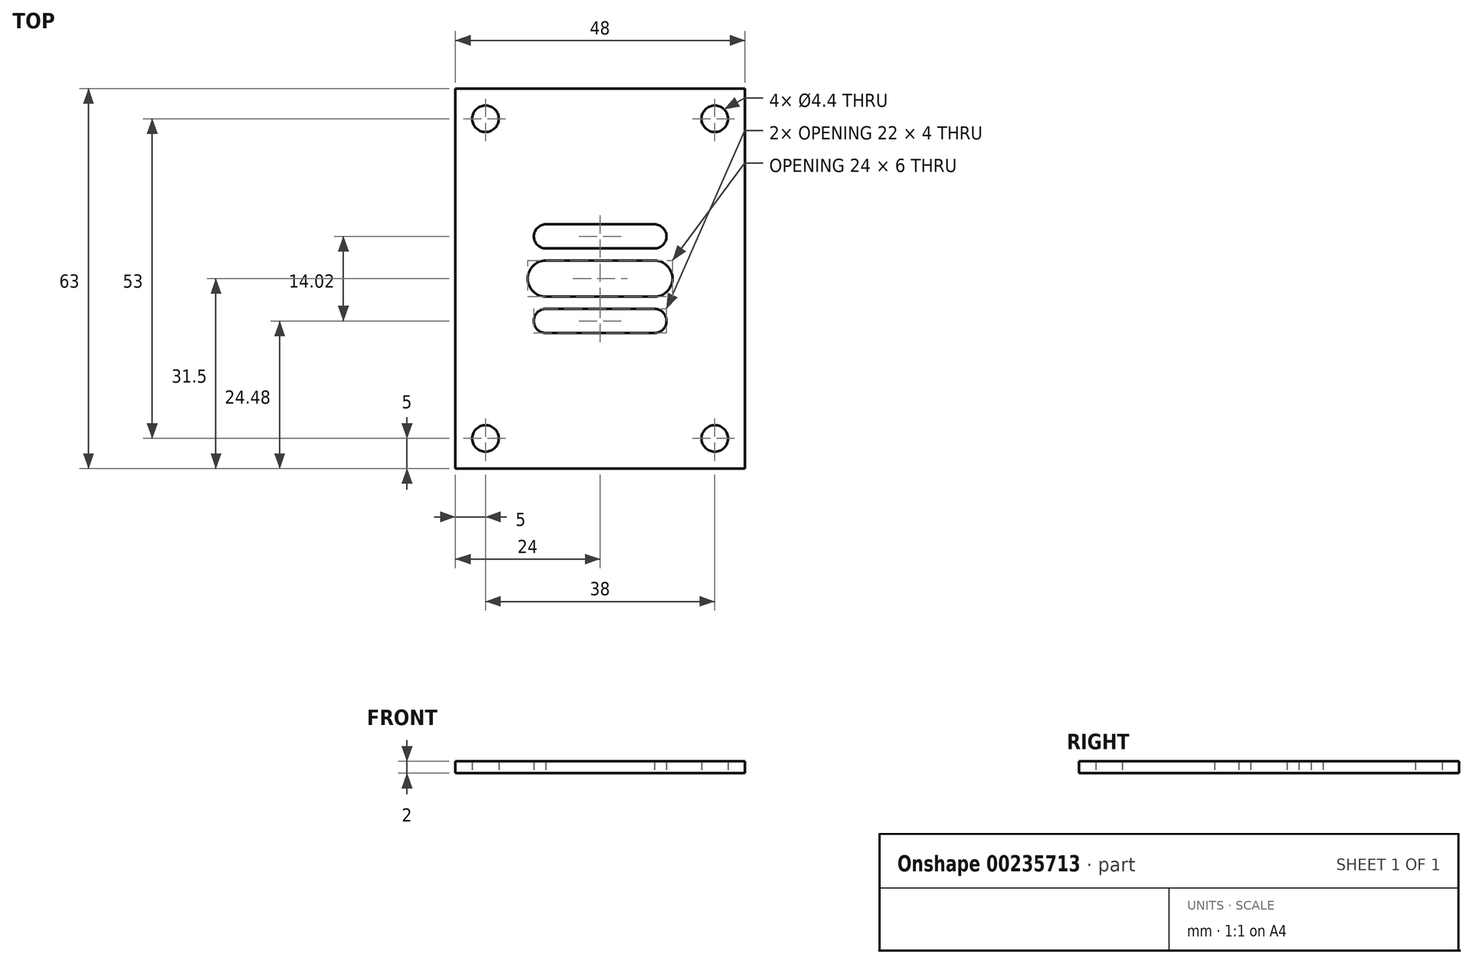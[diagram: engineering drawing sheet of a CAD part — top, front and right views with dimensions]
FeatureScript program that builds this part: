
annotation { "Feature Type Name" : "Feature", "Feature Type Description" : "" }
export const myFeature = defineFeature(function(context is Context, id is Id, definition is map)
    precondition{}
    {
        {
            var Q0;
            Q0=qCreatedBy(makeId("Top.planeOp"),FACE);
            var sketch = newSketch(context, id + "F0", { "sketchPlane" : qUnion([Q0])});
            skLineSegment(sketch, "E0.bottom", {"start": v(0, 0) * mm, "end": v(48, 0) * mm});
            skLineSegment(sketch, "E0.top", {"start": v(0, -63) * mm, "end": v(48, -63) * mm});
            skLineSegment(sketch, "E0.left", {"start": v(0, 0) * mm, "end": v(0, -63) * mm});
            skLineSegment(sketch, "E0.right", {"start": v(48, 0) * mm, "end": v(48, -63) * mm});
            skLineSegment(sketch, "E1", {"start": v(0, -31.5) * mm, "end": v(48, -31.5) * mm});
            skLineSegment(sketch, "E2", {"start": v(24, 0) * mm, "end": v(24, -63) * mm});
            skLineSegment(sketch, "E3.bottom", {"start": v(33, -28.5) * mm, "end": v(15, -28.5) * mm});
            skLineSegment(sketch, "E3.top", {"start": v(33, -34.5) * mm, "end": v(15, -34.5) * mm});
            skLineSegment(sketch, "E3.left", {"start": v(36, -31.5) * mm, "end": v(36, -31.5) * mm});
            skLineSegment(sketch, "E3.right", {"start": v(12, -31.5) * mm, "end": v(12, -31.5) * mm});
            skPoint(sketch, "E3.middle", {"position": v(24, -31.5) * mm});
            skPoint(sketch, "E4.visualSharp", {"position": v(12, -28.5) * mm});
            skArc(sketch, "E4.filletArc", {"start": v(15, -28.5) * mm, "mid": v(12.88, -29.38) * mm, "end": v(12, -31.5) * mm});
            skPoint(sketch, "E5.visualSharp", {"position": v(12, -34.5) * mm});
            skArc(sketch, "E5.filletArc", {"start": v(12, -31.5) * mm, "mid": v(12.88, -33.62) * mm, "end": v(15, -34.5) * mm});
            skPoint(sketch, "E6.visualSharp", {"position": v(36, -28.5) * mm});
            skArc(sketch, "E6.filletArc", {"start": v(36, -31.5) * mm, "mid": v(35.12, -29.38) * mm, "end": v(33, -28.5) * mm});
            skPoint(sketch, "E7.visualSharp", {"position": v(36, -34.5) * mm});
            skArc(sketch, "E7.filletArc", {"start": v(33, -34.5) * mm, "mid": v(35.12, -33.62) * mm, "end": v(36, -31.5) * mm});
            skLineSegment(sketch, "E8.bottom", {"start": v(15, -40.52) * mm, "end": v(33, -40.52) * mm});
            skLineSegment(sketch, "E8.top", {"start": v(15, -36.52) * mm, "end": v(33, -36.52) * mm});
            skLineSegment(sketch, "E8.left", {"start": v(13, -38.52) * mm, "end": v(13, -38.52) * mm});
            skLineSegment(sketch, "E8.right", {"start": v(35, -38.52) * mm, "end": v(35, -38.52) * mm});
            skPoint(sketch, "E8.middle", {"position": v(24, -38.52) * mm});
            skPoint(sketch, "E9.visualSharp", {"position": v(13, -36.52) * mm});
            skArc(sketch, "E9.filletArc", {"start": v(15, -36.52) * mm, "mid": v(13.59, -37.1) * mm, "end": v(13, -38.52) * mm});
            skPoint(sketch, "E10.visualSharp", {"position": v(13, -40.52) * mm});
            skArc(sketch, "E10.filletArc", {"start": v(13, -38.52) * mm, "mid": v(13.59, -39.94) * mm, "end": v(15, -40.52) * mm});
            skPoint(sketch, "E11.visualSharp", {"position": v(35, -40.52) * mm});
            skArc(sketch, "E11.filletArc", {"start": v(33, -40.52) * mm, "mid": v(34.41, -39.94) * mm, "end": v(35, -38.52) * mm});
            skPoint(sketch, "E12.visualSharp", {"position": v(35, -36.52) * mm});
            skArc(sketch, "E12.filletArc", {"start": v(35, -38.52) * mm, "mid": v(34.41, -37.1) * mm, "end": v(33, -36.52) * mm});
            skLineSegment(sketch, "E13.bottom", {"start": v(33, -26.5) * mm, "end": v(15, -26.5) * mm});
            skLineSegment(sketch, "E13.top", {"start": v(33, -22.5) * mm, "end": v(15, -22.5) * mm});
            skLineSegment(sketch, "E13.left", {"start": v(35, -24.5) * mm, "end": v(35, -24.5) * mm});
            skLineSegment(sketch, "E13.right", {"start": v(13, -24.5) * mm, "end": v(13, -24.5) * mm});
            skPoint(sketch, "E13.middle", {"position": v(24, -24.5) * mm});
            skPoint(sketch, "E14.visualSharp", {"position": v(13, -22.5) * mm});
            skArc(sketch, "E14.filletArc", {"start": v(15, -22.5) * mm, "mid": v(13.59, -23.1) * mm, "end": v(13, -24.5) * mm});
            skPoint(sketch, "E15.visualSharp", {"position": v(13, -26.5) * mm});
            skArc(sketch, "E15.filletArc", {"start": v(13, -24.5) * mm, "mid": v(13.59, -25.9) * mm, "end": v(15, -26.5) * mm});
            skPoint(sketch, "E16.visualSharp", {"position": v(35, -22.5) * mm});
            skArc(sketch, "E16.filletArc", {"start": v(35, -24.5) * mm, "mid": v(34.41, -23.1) * mm, "end": v(33, -22.5) * mm});
            skPoint(sketch, "E17.visualSharp", {"position": v(35, -26.5) * mm});
            skArc(sketch, "E17.filletArc", {"start": v(33, -26.5) * mm, "mid": v(34.41, -25.9) * mm, "end": v(35, -24.5) * mm});
            skLineSegment(sketch, "E18.bottom", {"start": v(5, -5) * mm, "end": v(43, -5) * mm, "construction": true});
            skLineSegment(sketch, "E18.top", {"start": v(5, -58) * mm, "end": v(43, -58) * mm, "construction": true});
            skLineSegment(sketch, "E18.left", {"start": v(5, -5) * mm, "end": v(5, -58) * mm, "construction": true});
            skLineSegment(sketch, "E18.right", {"start": v(43, -5) * mm, "end": v(43, -58) * mm, "construction": true});
            skSolve(sketch);
        }
        {
            var Q0;
            Q0 = qSketchRegion(id + "F0", true);
            extrude(context, id + "F1", {"entities" : qUnion([Q0]), "depth" : 2 * mm});
        }
        {
            var Q0;
            Q0=sQuery(id+"F0.wireOp",VERTEX,"E18.left.start");
            var Q1;
            Q1=sQuery(id+"F0.wireOp",VERTEX,"E18.bottom.end");
            var Q2;
            Q2=sQuery(id+"F0.wireOp",VERTEX,"E18.top.end");
            var Q3;
            Q3=sQuery(id+"F0.wireOp",VERTEX,"E18.left.end");
            var Q4;
            Q4=makeQuery(id+"F1.opExtrude","SWEPT_BODY",BODY,{"disambiguationData":[OSD([sQuery(id+"F0.wireOp",EDGE,"E0.bottom"),sQuery(id+"F0.wireOp",EDGE,"E0.top"),sQuery(id+"F0.wireOp",EDGE,"E0.left"),sQuery(id+"F0.wireOp",EDGE,"E0.right"),sQuery(id+"F0.wireOp",EDGE,"E3.bottom"),sQuery(id+"F0.wireOp",EDGE,"E3.top"),sQuery(id+"F0.wireOp",EDGE,"E4.filletArc"),sQuery(id+"F0.wireOp",EDGE,"E5.filletArc"),sQuery(id+"F0.wireOp",EDGE,"E6.filletArc"),sQuery(id+"F0.wireOp",EDGE,"E7.filletArc"),sQuery(id+"F0.wireOp",EDGE,"E8.bottom"),sQuery(id+"F0.wireOp",EDGE,"E8.top"),sQuery(id+"F0.wireOp",EDGE,"E9.filletArc"),sQuery(id+"F0.wireOp",EDGE,"E10.filletArc"),sQuery(id+"F0.wireOp",EDGE,"E11.filletArc"),sQuery(id+"F0.wireOp",EDGE,"E12.filletArc"),sQuery(id+"F0.wireOp",EDGE,"E13.bottom"),sQuery(id+"F0.wireOp",EDGE,"E13.top"),sQuery(id+"F0.wireOp",EDGE,"E13.left"),sQuery(id+"F0.wireOp",EDGE,"E13.right"),sQuery(id+"F0.wireOp",EDGE,"E14.filletArc"),sQuery(id+"F0.wireOp",EDGE,"E15.filletArc"),sQuery(id+"F0.wireOp",EDGE,"E16.filletArc"),sQuery(id+"F0.wireOp",EDGE,"E17.filletArc")])]});
            hole(context, id + "F2", {"style" : HoleStyle.SIMPLE, "endStyle" : HoleEndStyle.BLIND, "oppositeDirection" : true, "standardTappedOrClearance" : lookupTablePath({ "standard" : "ISO", "fit" : "Normal", "size" : "M4", "type" : "Clearance" }), "standardBlindInLast" : lookupTablePath({ "fit" : "Standard", "standard" : "ISO", "size" : "M4", "type" : "Clearance" }), "holeDiameter" : 4.4 * mm, "holeDepth" : 5 * mm, "tappedDepth" : 9 * mm, "tapClearance" : 3, "startFromSketch" : true, "locations" : qUnion([Q0, Q1, Q2, Q3]), "scope" : qUnion([Q4])});
        }
    });
